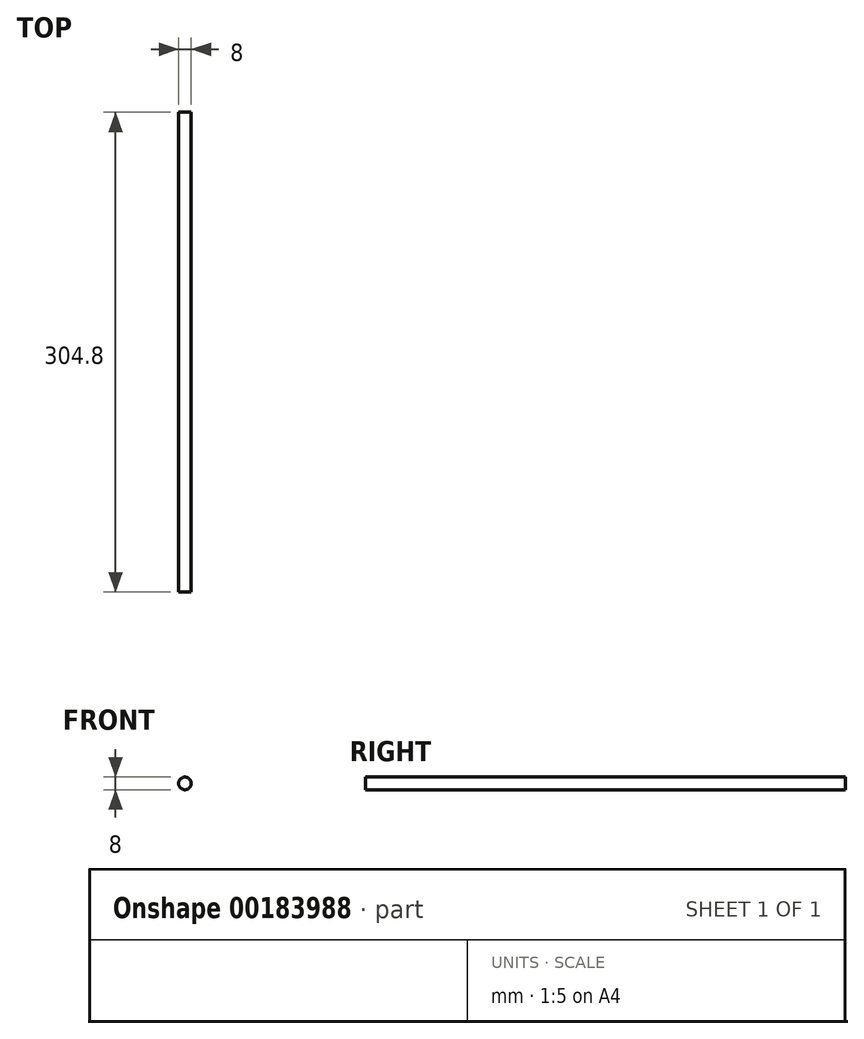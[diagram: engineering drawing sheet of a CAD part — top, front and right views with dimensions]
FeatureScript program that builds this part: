
annotation { "Feature Type Name" : "Feature", "Feature Type Description" : "" }
export const myFeature = defineFeature(function(context is Context, id is Id, definition is map)
    precondition{}
    {
        {
            var Q0;
            Q0=qCreatedBy(makeId("Front.planeOp"),FACE);
            var sketch = newSketch(context, id + "F0", { "sketchPlane" : qUnion([Q0])});
            skCircle(sketch, "E0", {"center": v(0, 0) * mm, "radius": 4 * mm});
            skSolve(sketch);
        }
        {
            var Q0;
            Q0 = qSketchRegion(id + "F0", true);
            extrude(context, id + "F1", {"entities" : qUnion([Q0]), "oppositeDirection" : true, "depth" : 304.8 * mm});
        }
    });
